# Revit family: SE-200_A_GENERADO
name_source: partatom
category: Equipos especializados
revit_build: Autodesk Revit 2016 (Build: 20151007_0715(x64)
units: mm (PartAtom-declared; Revit-internal decimal feet)

## family parameters
Compartido = No
Corte con vacíos al cargar = No
Cota de conector redondo = Diámetro de uso
Número OmniClass = 23.21.21.47
Punto de cálculo de habitación = No
Se basa en plano de trabajo = No
Siempre vertical = Sí
Tipo de pieza = Normal

## types (7) — shared parameters
Depth = 431 mm  [stored 1.41404 ft]
Fabricante = SAMMIC S.L.
Foodservice Equipment Identifier = Sí
Phase = 1
Revision Code = 1
URL = https://www.sammic.com
URL Cutsheet = http://www.sammic.com
Width = 337 mm  [stored 1.10564 ft]

## per-type parameters (varying)
| type | Comentarios de tipo | Conn Plug | Cycle | FL Amps | Height | Modelo | Specification by Manufacturer | Volts | Weight in Pounds |
| Vacuum packing machine SE-204 230/50-60/1 | Tabletop model. 4 m³/h. 280 mm | EU (SCHUKO 2P+G) | 50 Hz | 1 A | 307 mm  [stored 1.00722 ft] | 1140620 | 280 mm sealing bar.
4 m³/h Busch vacuum pump.
Vacuum controlled by sensor. | 230 V | 53.4 |
| Vacuum packing machine SE-204 120/50-60/1 | Tabletop model. 5 m³/h. 280 mm | USA (NEMA 5-15P / 2P+G) | 60 Hz | 2 A | 307 mm  [stored 1.00722 ft] | 1140621 | 280 mm sealing bar.
5 m³/h Busch vacuum pump.
Vacuum controlled by sensor. | 120 V | 53.4 |
| Vacuum packing machine SE-204 230/50-60/1 KSA | Tabletop model. 4 m³/h. 280 mm | UK (BS 1363 13A / 2P+G) | 50 Hz | 1 A | 307 mm  [stored 1.00722 ft] | 1140625 | 280 mm sealing bar.
4 m³/h Busch vacuum pump.
Vacuum controlled by sensor. | 230 V | 53.4 |
| Vacuum packing machine SE-206 230/50-60/1 | Tabletop model. 6 m³/h. 280 mm. | EU (SCHUKO 2P+G) | 50 Hz | 4 A | 307 mm  [stored 1.00722 ft] | 1140622 | 280 mm. sealing bar.
6 m³/h Busch vacuum pump.
Vacuum controlled by sensor. | 230 V | 70.5 |
| Vacuum packing machine SE-208 230/50-60/1 | Tabletop model. 8 m³/h. 280 mm | EU (SCHUKO 2P+G) | 50 Hz | 3 A | 331 mm  [stored 1.08596 ft] | 1141080 | 280 mm sealing bar.
8 m³/h Busch vacuum pump.
Vacuum controlled by sensor. | 230 V | 70.5 |
| Vacuum packing machine SE-208 120/50-60/1 | Tabletop model. 8 m³/h. 280 mm | USA (NEMA 5-15P / 2P+G) | 60 Hz | 6 A | 331 mm  [stored 1.08596 ft] | 1141081 | 280 mm sealing bar.
8 m³/h Busch vacuum pump.
Vacuum controlled by sensor. | 120 V | 70.5 |
| Vacuum packing machine SE-208 230/50-60/1 KSA | Tabletop model. 8 m³/h. 280 mm | UK (BS 1363 13A / 2P+G) | 50 Hz | 3 A | 331 mm  [stored 1.08596 ft] | 1141085 | 280 mm sealing bar.
8 m³/h Busch vacuum pump.
Vacuum controlled by sensor. | 230 V | 70.5 |

note: column(s) folded — value = type name in every type: Descripción

note: [stored X ft] marks values corroborated as IEEE doubles in the binary element streams (Revit-internal decimal feet)
